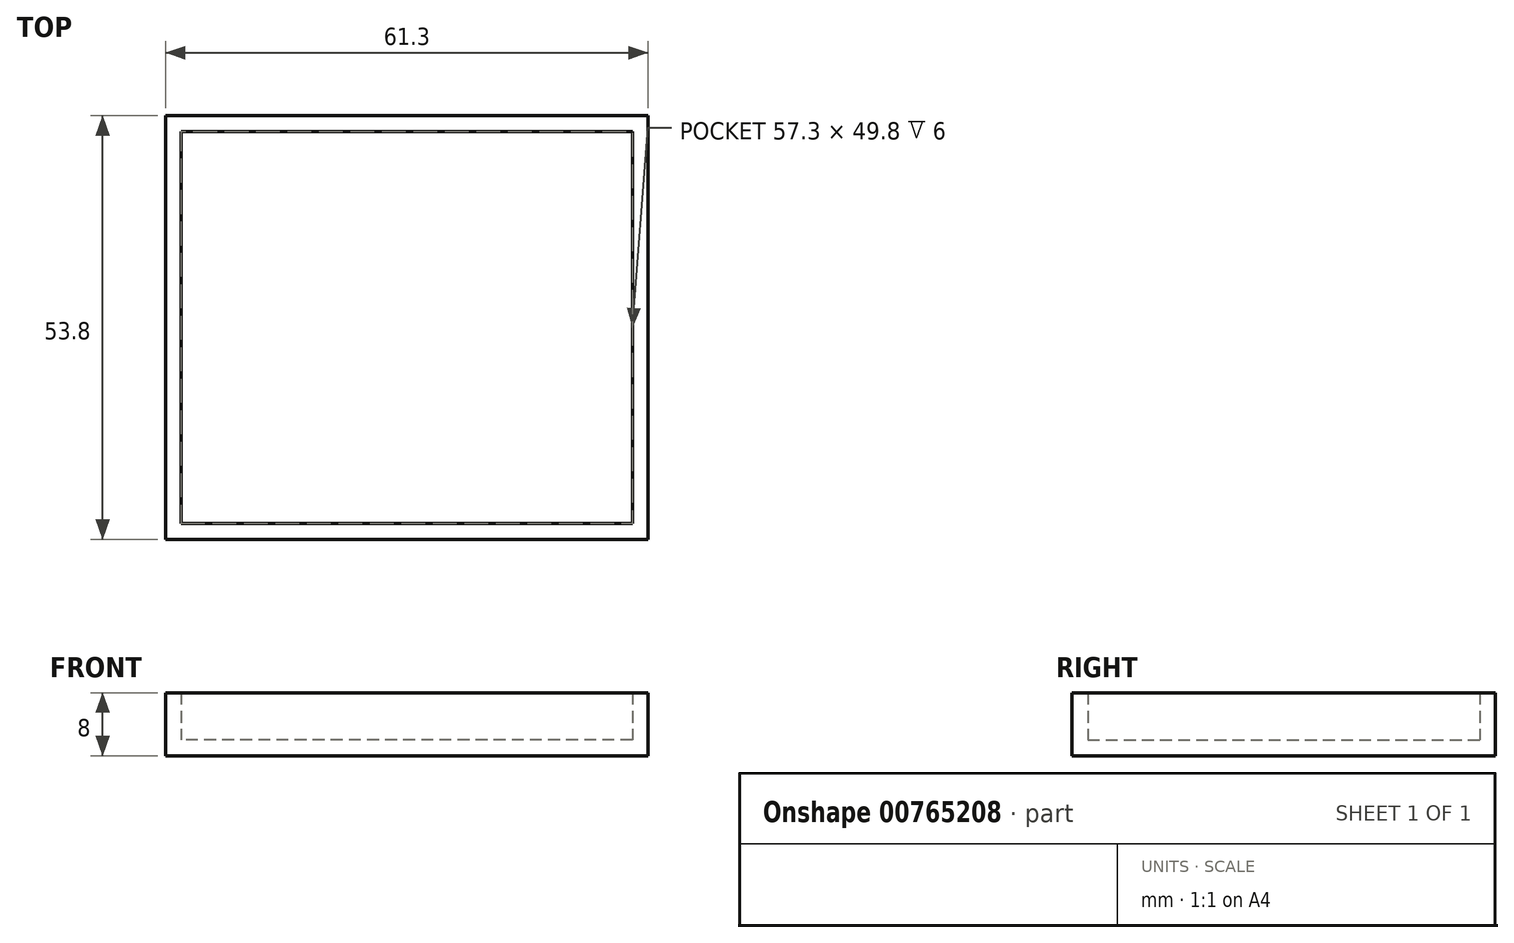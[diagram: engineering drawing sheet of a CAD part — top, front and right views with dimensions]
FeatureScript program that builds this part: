
annotation { "Feature Type Name" : "Feature", "Feature Type Description" : "" }
export const myFeature = defineFeature(function(context is Context, id is Id, definition is map)
    precondition{}
    {
        {
            assignVariable(context, id + "F0", {"name" : "T", "anyValue" : 1.8});
        }
        {
            var Q0;
            Q0=qCreatedBy(makeId("Top.planeOp"),FACE);
            var sketch = newSketch(context, id + "F1", { "sketchPlane" : qUnion([Q0])});
            skLineSegment(sketch, "E0.bottom", {"start": v(30.65, -26.9) * mm, "end": v(-30.65, -26.9) * mm});
            skLineSegment(sketch, "E0.top", {"start": v(30.65, 26.9) * mm, "end": v(-30.65, 26.9) * mm});
            skLineSegment(sketch, "E0.left", {"start": v(30.65, -26.9) * mm, "end": v(30.65, 26.9) * mm});
            skLineSegment(sketch, "E0.right", {"start": v(-30.65, -26.9) * mm, "end": v(-30.65, 26.9) * mm});
            skPoint(sketch, "E0.middle", {"position": v(0, 0) * mm});
            skSolve(sketch);
        }
        {
            var Q0;
            Q0 = qSketchRegion(id + "F1", true);
            extrude(context, id + "F2", {"entities" : qUnion([Q0]), "depth" : (6.2 + getVariable(context, 'T')) * mm, "offsetDistance" : 25 * mm});
        }
        {
            var Q0;
            Q0=makeQuery(id+"F2.opExtrude","CAP_FACE",FACE,{"disambiguationData":[OSD([sQuery(id+"F1.wireOp",EDGE,"E0.bottom"),sQuery(id+"F1.wireOp",EDGE,"E0.top"),sQuery(id+"F1.wireOp",EDGE,"E0.left"),sQuery(id+"F1.wireOp",EDGE,"E0.right")])],"isStart":false});
            shell(context, id + "F3", {"entities" : qUnion([Q0]), "thickness" : 2 * mm});
        }
    });
